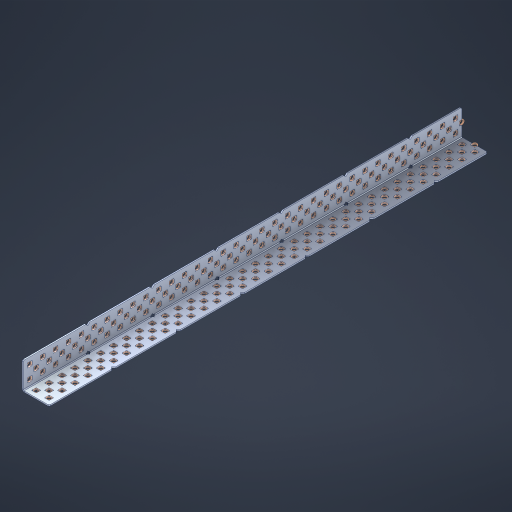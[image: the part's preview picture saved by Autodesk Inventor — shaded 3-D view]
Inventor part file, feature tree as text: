
AUTODESK INVENTOR PART (.ipt)
format: ipt  version: 2023 (Build 270158000, 158)  size: 2,273,792 bytes
history: native  units: in
note: dims shown in document units (in); Inventor stores cm internally (conversion verified against a paired STEP export)
features: other x210, extrude x202, sheet_metal_op x8, sketch x7, pattern_linear x2, mirror x1, chamfer x1
ambient origin geometry x8: Origin, YZ Plane, XZ Plane, XY Plane, X Axis, Y Axis, Z Axis, Center Point
bodies: Solid1 (feature_tree), Body (feature_tree)
feature tree (431):
  sheet_metal_op  "Flanges"
  sheet_metal_op  "Body Pattern"
  pattern_linear  "Center Pattern"  Spacing1=1.0in  [1 undecoded]
  other  "Arc Length"
  pattern_linear  "Notch Pattern"  Spacing1=0.1875in  [1 undecoded]
  other  "Diagonal Plane"
  mirror  "Everything Mirrored"
  chamfer  "End Chamfer"
  sketch  "Sketch1"  dims[d0=1.0in]
  other  "Plate1"
  sketch  "Sketch2"  dims[d1=17.0in]
  other  "Plate2"
  sheet_metal_op  "Bend1"
  sheet_metal_op  "Corner1"
  sketch  "Sketch8"  dims[d2=0.0469in]
  sketch  "Sketch9"  dims[d3=0.0469in]
  other  "Srf91"
  sheet_metal_op  "Body Pattern Sketch"
  other  "Srf92"
  sketch  "Sketch13"  dims[d4=0.0234in]
  sketch  "Sketch15"  dims[d5=0.0938in]
  sketch  "Sketch16"  dims[d6=0.0469in d7=1.0in d8=90.0deg d9=0.0312in d10=0.1875in d11=0.0469in d12=0.0469in d49=0.182in d50=0.02in d52=0.25in d53=0.0469in d54=0.0in d55=0.172in d56=1.0in d57=0.0in d60=13.3858in d62=0.5in d63=0.7874in d65=0.5in d85=0.1473in d86=0.1659in d89=0.0469in d90=0.0in d91=0.04in d92=0.0491in d95=2.5in d96=0.04in d97=0.25in d98=45.0deg d99=0.25in d106=0.182in d107=0.02in d108=0.5in d110=0.0469in d111=0.0in d112=0.172in d113=0.5in d114=0.0in d117=0.5in d123=0.25in d125=0.25in d126=0.0491in d127=0.1227in d128=0.08in d129=0.04in d130=2.5in]
  other  "Srf786"
  other  "Srf856"
  other  "Srf857"
  other  "Srf858"
  other  "Srf859"
  other  "Srf860"
  other  "Srf861"
  other  "Srf889"
  other  "Srf890"
  other  "Srf891"
  other  "Srf1275"
  other  "Srf1276"
  other  "Srf1278"
  other  "Srf1279"
  other  "Srf1280"
  other  "Srf1281"
  other  "Srf1282"
  other  "Srf1283"
  other  "Srf1277"
  other  "Srf1285"
  other  "Srf1286"
  other  "Srf1287"
  other  "Srf1383"
  other  "Srf1384"
  other  "Srf1385"
  other  "Srf1386"
  other  "Srf1387"
  other  "Srf1388"
  other  "Srf1389"
  other  "Srf1390"
  other  "Srf1391"
  other  "Srf1392"
  other  "Srf1393"
  other  "Srf1394"
  other  "Srf1395"
  other  "Srf1396"
  other  "Srf1397"
  other  "Srf1398"
  other  "Srf1399"
  other  "Srf1400"
  other  "Srf1401"
  other  "Srf1402"
  other  "Srf1403"
  other  "Srf1404"
  other  "Srf1405"
  other  "Srf1406"
  other  "Srf1407"
  other  "Srf1408"
  other  "Srf1409"
  other  "Srf1410"
  other  "Srf1411"
  other  "Srf1412"
  other  "Srf1413"
  other  "Srf1414"
  other  "Srf1415"
  other  "Srf1416"
  other  "Srf1417"
  other  "Srf1418"
  other  "Srf1419"
  other  "Srf1420"
  other  "Srf1421"
  other  "Srf1422"
  other  "Srf1423"
  other  "Srf1424"
  other  "Srf1425"
  other  "Srf1426"
  other  "Srf1427"
  other  "Srf1428"
  other  "Srf1429"
  other  "Srf1430"
  other  "Srf1431"
  other  "Srf1432"
  other  "Srf1433"
  other  "Srf1434"
  other  "Srf1435"
  other  "Srf1436"
  other  "Srf1437"
  other  "Srf1438"
  other  "Srf1439"
  other  "Srf1440"
  other  "Srf1441"
  other  "Srf1442"
  other  "Srf1445"
  other  "Srf1446"
  other  "Srf1447"
  other  "Srf1448"
  other  "Srf1449"
  other  "Srf1450"
  other  "Srf1451"
  other  "Srf1452"
  other  "Srf1453"
  other  "Srf1454"
  other  "Srf1455"
  other  "Srf1456"
  other  "Srf1457"
  other  "Srf1458"
  other  "Srf1459"
  other  "Srf1460"
  other  "Srf1461"
  other  "Srf1462"
  other  "Srf1463"
  other  "Srf1464"
  other  "Srf1465"
  other  "Srf1466"
  other  "Srf1467"
  other  "Srf1468"
  other  "Srf1469"
  other  "Srf1470"
  other  "Srf1471"
  other  "Srf1472"
  other  "Srf1473"
  other  "Srf1474"
  other  "Srf1475"
  other  "Srf1476"
  other  "Srf1477"
  other  "Srf1478"
  other  "Srf1479"
  other  "Srf1480"
  other  "Srf1481"
  other  "Srf1482"
  other  "Srf1483"
  other  "Srf1484"
  other  "Srf1485"
  other  "Srf1486"
  other  "Srf1487"
  other  "Srf1488"
  other  "Srf1489"
  other  "Srf1490"
  other  "Srf1491"
  other  "Srf1492"
  other  "Srf1493"
  other  "Srf1494"
  other  "Srf1495"
  other  "Srf1496"
  other  "Srf1497"
  other  "Srf1498"
  other  "Srf1499"
  other  "Srf1500"
  other  "Srf1501"
  other  "Srf1502"
  other  "Srf1503"
  other  "Srf1504"
  other  "Srf1505"
  other  "Srf1506"
  other  "Srf1507"
  other  "Srf1508"
  other  "Srf1509"
  other  "Srf1510"
  other  "Srf1511"
  other  "Srf1512"
  other  "Srf1513"
  other  "Srf1514"
  other  "Srf1515"
  other  "Srf1516"
  other  "Srf1517"
  other  "Srf1518"
  other  "Srf1519"
  other  "Srf1520"
  other  "Srf1521"
  other  "Srf1522"
  other  "Srf1523"
  other  "Srf1524"
  other  "Srf1525"
  other  "Srf1526"
  other  "Srf1527"
  other  "Srf1528"
  other  "Srf1529"
  other  "Srf1530"
  other  "Srf1531"
  other  "Srf1532"
  other  "Srf1533"
  other  "Srf1534"
  other  "Srf1537"
  other  "Srf1538"
  other  "Srf1539"
  other  "Srf1540"
  other  "Srf1541"
  other  "Srf1542"
  other  "Srf1543"
  other  "Srf1544"
  other  "Srf1545"
  other  "Srf1546"
  other  "Srf1547"
  other  "Srf1548"
  other  "Srf1549"
  other  "Srf1550"
  other  "Srf1551"
  other  "Srf1552"
  other  "Srf1553"
  other  "Srf1554"
  other  "Srf1555"
  other  "Srf1556"
  other  "Srf1557"
  other  "Srf1558"
  other  "Srf1559"
  other  "Srf1560"
  other  "Srf1561"
  other  "Srf1562"
  other  "Srf1563"
  other  "Srf1564"
  other  "Srf1565"
  other  "Srf1566"
  sheet_metal_op  "Body Stamp"
  sheet_metal_op  "Body Circle"
  other  "Center Stamp"
  other  "Center Circle"
  sheet_metal_op  "Notch"
  extrude  "ExtrusionSrf92"  Depth=0.0469in
  extrude  "ExtrusionSrf856"  Depth=0.0469in
  extrude  "ExtrusionSrf857"  Depth=0.182in
  extrude  "ExtrusionSrf858"  Depth=0.02in
  extrude  "ExtrusionSrf859"  Depth=0.25in
  extrude  "ExtrusionSrf860"  Depth=0.0469in
  extrude  "ExtrusionSrf861"  TaperAngle=0.0deg  [1 undecoded]
  extrude  "ExtrusionSrf889"  Depth=2.5in
  extrude  "ExtrusionSrf890"  Depth=1.0in TaperAngle=0.0deg
  extrude  "ExtrusionSrf891"  Depth=2.5in
  extrude  "ExtrusionSrf1275"  Depth=0.5in
  extrude  "ExtrusionSrf1276"  Depth=2.5in
  extrude  "ExtrusionSrf1277"  Depth=2.5in
  extrude  "ExtrusionSrf1278"  Depth=0.0469in
  extrude  "ExtrusionSrf1279"  Depth=2.5in TaperAngle=0.0deg
  extrude  "ExtrusionSrf1280"  Depth=2.5in
  extrude  "ExtrusionSrf1281"  Depth=0.25in TaperAngle=45.0deg
  extrude  "ExtrusionSrf1282"  Depth=0.25in
  extrude  "ExtrusionSrf1345"  Depth=0.182in
  extrude  "ExtrusionSrf1346"  Depth=0.02in
  extrude  "ExtrusionSrf1347"  Depth=0.5in
  extrude  "ExtrusionSrf1348"  Depth=0.0469in
  extrude  "ExtrusionSrf1383"  TaperAngle=0.0deg  [1 undecoded]
  extrude  "ExtrusionSrf1384"  Depth=2.5in
  extrude  "ExtrusionSrf1385"  Depth=0.5in TaperAngle=0.0deg
  extrude  "ExtrusionSrf1386"  Depth=0.5in
  extrude  "ExtrusionSrf1387"  Depth=0.25in
  extrude  "ExtrusionSrf1388"  Depth=0.25in
  extrude  "ExtrusionSrf1389"  Depth=2.5in
  extrude  "ExtrusionSrf1390"  Depth=2.5in
  extrude  "ExtrusionSrf1391"  Depth=2.5in
  extrude  "ExtrusionSrf1392"  Depth=2.5in
  extrude  "ExtrusionSrf1393"  Depth=2.5in
  extrude  "ExtrusionSrf1394"  [1 undecoded]
  extrude  "ExtrusionSrf1395"  [1 undecoded]
  extrude  "ExtrusionSrf1396"  [1 undecoded]
  extrude  "ExtrusionSrf1397"  [1 undecoded]
  extrude  "ExtrusionSrf1398"  [1 undecoded]
  extrude  "ExtrusionSrf1399"  [1 undecoded]
  extrude  "ExtrusionSrf1400"  [1 undecoded]
  extrude  "ExtrusionSrf1401"  [1 undecoded]
  extrude  "ExtrusionSrf1402"  [1 undecoded]
  extrude  "ExtrusionSrf1403"  [1 undecoded]
  extrude  "ExtrusionSrf1404"  [1 undecoded]
  extrude  "ExtrusionSrf1405"  [1 undecoded]
  extrude  "ExtrusionSrf1406"  [1 undecoded]
  extrude  "ExtrusionSrf1407"  [1 undecoded]
  extrude  "ExtrusionSrf1408"  [1 undecoded]
  extrude  "ExtrusionSrf1409"  [1 undecoded]
  extrude  "ExtrusionSrf1410"  [1 undecoded]
  extrude  "ExtrusionSrf1411"  [1 undecoded]
  extrude  "ExtrusionSrf1412"  [1 undecoded]
  extrude  "ExtrusionSrf1413"  [1 undecoded]
  extrude  "ExtrusionSrf1414"  [1 undecoded]
  extrude  "ExtrusionSrf1415"  [1 undecoded]
  extrude  "ExtrusionSrf1416"  [1 undecoded]
  extrude  "ExtrusionSrf1417"  [1 undecoded]
  extrude  "ExtrusionSrf1418"  [1 undecoded]
  extrude  "ExtrusionSrf1419"  [1 undecoded]
  extrude  "ExtrusionSrf1420"  [1 undecoded]
  extrude  "ExtrusionSrf1421"  [1 undecoded]
  extrude  "ExtrusionSrf1422"  [1 undecoded]
  extrude  "ExtrusionSrf1423"  [1 undecoded]
  extrude  "ExtrusionSrf1424"  [1 undecoded]
  extrude  "ExtrusionSrf1425"  [1 undecoded]
  extrude  "ExtrusionSrf1426"  [1 undecoded]
  extrude  "ExtrusionSrf1427"  [1 undecoded]
  extrude  "ExtrusionSrf1428"  [1 undecoded]
  extrude  "ExtrusionSrf1429"  [1 undecoded]
  extrude  "ExtrusionSrf1430"  [1 undecoded]
  extrude  "ExtrusionSrf1431"  [1 undecoded]
  extrude  "ExtrusionSrf1432"  [1 undecoded]
  extrude  "ExtrusionSrf1433"  [1 undecoded]
  extrude  "ExtrusionSrf1434"  [1 undecoded]
  extrude  "ExtrusionSrf1435"  [1 undecoded]
  extrude  "ExtrusionSrf1436"  [1 undecoded]
  extrude  "ExtrusionSrf1437"  [1 undecoded]
  extrude  "ExtrusionSrf1438"  [1 undecoded]
  extrude  "ExtrusionSrf1439"  [1 undecoded]
  extrude  "ExtrusionSrf1440"  [1 undecoded]
  extrude  "ExtrusionSrf1441"  [1 undecoded]
  extrude  "ExtrusionSrf1442"  [1 undecoded]
  extrude  "ExtrusionSrf1445"  [1 undecoded]
  extrude  "ExtrusionSrf1446"  [1 undecoded]
  extrude  "ExtrusionSrf1447"  [1 undecoded]
  extrude  "ExtrusionSrf1448"  [1 undecoded]
  extrude  "ExtrusionSrf1449"  [1 undecoded]
  extrude  "ExtrusionSrf1450"  [1 undecoded]
  extrude  "ExtrusionSrf1451"  [1 undecoded]
  extrude  "ExtrusionSrf1452"  [1 undecoded]
  extrude  "ExtrusionSrf1453"  [1 undecoded]
  extrude  "ExtrusionSrf1454"  [1 undecoded]
  extrude  "ExtrusionSrf1455"  [1 undecoded]
  extrude  "ExtrusionSrf1456"  [1 undecoded]
  extrude  "ExtrusionSrf1457"  [1 undecoded]
  extrude  "ExtrusionSrf1458"  [1 undecoded]
  extrude  "ExtrusionSrf1459"  [1 undecoded]
  extrude  "ExtrusionSrf1460"  [1 undecoded]
  extrude  "ExtrusionSrf1461"  [1 undecoded]
  extrude  "ExtrusionSrf1462"  [1 undecoded]
  extrude  "ExtrusionSrf1463"  [1 undecoded]
  extrude  "ExtrusionSrf1464"  [1 undecoded]
  extrude  "ExtrusionSrf1465"  [1 undecoded]
  extrude  "ExtrusionSrf1466"  [1 undecoded]
  extrude  "ExtrusionSrf1467"  [1 undecoded]
  extrude  "ExtrusionSrf1468"  [1 undecoded]
  extrude  "ExtrusionSrf1469"  [1 undecoded]
  extrude  "ExtrusionSrf1470"  [1 undecoded]
  extrude  "ExtrusionSrf1471"  [1 undecoded]
  extrude  "ExtrusionSrf1472"  [1 undecoded]
  extrude  "ExtrusionSrf1473"  [1 undecoded]
  extrude  "ExtrusionSrf1474"  [1 undecoded]
  extrude  "ExtrusionSrf1475"  [1 undecoded]
  extrude  "ExtrusionSrf1476"  [1 undecoded]
  extrude  "ExtrusionSrf1477"  [1 undecoded]
  extrude  "ExtrusionSrf1478"  [1 undecoded]
  extrude  "ExtrusionSrf1479"  [1 undecoded]
  extrude  "ExtrusionSrf1480"  [1 undecoded]
  extrude  "ExtrusionSrf1481"  [1 undecoded]
  extrude  "ExtrusionSrf1482"  [1 undecoded]
  extrude  "ExtrusionSrf1483"  [1 undecoded]
  extrude  "ExtrusionSrf1484"  [1 undecoded]
  extrude  "ExtrusionSrf1485"  [1 undecoded]
  extrude  "ExtrusionSrf1486"  [1 undecoded]
  extrude  "ExtrusionSrf1487"  [1 undecoded]
  extrude  "ExtrusionSrf1488"  [1 undecoded]
  extrude  "ExtrusionSrf1489"  [1 undecoded]
  extrude  "ExtrusionSrf1490"  [1 undecoded]
  extrude  "ExtrusionSrf1491"  [1 undecoded]
  extrude  "ExtrusionSrf1492"  [1 undecoded]
  extrude  "ExtrusionSrf1493"  [1 undecoded]
  extrude  "ExtrusionSrf1494"  [1 undecoded]
  extrude  "ExtrusionSrf1495"  [1 undecoded]
  extrude  "ExtrusionSrf1496"  [1 undecoded]
  extrude  "ExtrusionSrf1497"  [1 undecoded]
  extrude  "ExtrusionSrf1498"  [1 undecoded]
  extrude  "ExtrusionSrf1499"  [1 undecoded]
  extrude  "ExtrusionSrf1500"  [1 undecoded]
  extrude  "ExtrusionSrf1501"  [1 undecoded]
  extrude  "ExtrusionSrf1502"  [1 undecoded]
  extrude  "ExtrusionSrf1503"  [1 undecoded]
  extrude  "ExtrusionSrf1504"  [1 undecoded]
  extrude  "ExtrusionSrf1505"  [1 undecoded]
  extrude  "ExtrusionSrf1506"  [1 undecoded]
  extrude  "ExtrusionSrf1507"  [1 undecoded]
  extrude  "ExtrusionSrf1508"  [1 undecoded]
  extrude  "ExtrusionSrf1509"  [1 undecoded]
  extrude  "ExtrusionSrf1510"  [1 undecoded]
  extrude  "ExtrusionSrf1511"  [1 undecoded]
  extrude  "ExtrusionSrf1512"  [1 undecoded]
  extrude  "ExtrusionSrf1513"  [1 undecoded]
  extrude  "ExtrusionSrf1514"  [1 undecoded]
  extrude  "ExtrusionSrf1515"  [1 undecoded]
  extrude  "ExtrusionSrf1516"  [1 undecoded]
  extrude  "ExtrusionSrf1517"  [1 undecoded]
  extrude  "ExtrusionSrf1518"  [1 undecoded]
  extrude  "ExtrusionSrf1519"  [1 undecoded]
  extrude  "ExtrusionSrf1520"  [1 undecoded]
  extrude  "ExtrusionSrf1521"  [1 undecoded]
  extrude  "ExtrusionSrf1522"  [1 undecoded]
  extrude  "ExtrusionSrf1523"  [1 undecoded]
  extrude  "ExtrusionSrf1524"  [1 undecoded]
  extrude  "ExtrusionSrf1525"  [1 undecoded]
  extrude  "ExtrusionSrf1526"  [1 undecoded]
  extrude  "ExtrusionSrf1527"  [1 undecoded]
  extrude  "ExtrusionSrf1528"  [1 undecoded]
  extrude  "ExtrusionSrf1529"  [1 undecoded]
  extrude  "ExtrusionSrf1530"  [1 undecoded]
  extrude  "ExtrusionSrf1531"  [1 undecoded]
  extrude  "ExtrusionSrf1532"  [1 undecoded]
  extrude  "ExtrusionSrf1533"  [1 undecoded]
  extrude  "ExtrusionSrf1534"  [1 undecoded]
  extrude  "ExtrusionSrf1537"  [1 undecoded]
  extrude  "ExtrusionSrf1538"  [1 undecoded]
  extrude  "ExtrusionSrf1539"  [1 undecoded]
  extrude  "ExtrusionSrf1540"  [1 undecoded]
  extrude  "ExtrusionSrf1541"  [1 undecoded]
  extrude  "ExtrusionSrf1542"  [1 undecoded]
  extrude  "ExtrusionSrf1543"  [1 undecoded]
  extrude  "ExtrusionSrf1544"  [1 undecoded]
  extrude  "ExtrusionSrf1545"  [1 undecoded]
  extrude  "ExtrusionSrf1546"  [1 undecoded]
  extrude  "ExtrusionSrf1547"  [1 undecoded]
  extrude  "ExtrusionSrf1548"  [1 undecoded]
  extrude  "ExtrusionSrf1549"  [1 undecoded]
  extrude  "ExtrusionSrf1550"  [1 undecoded]
  extrude  "ExtrusionSrf1551"  [1 undecoded]
  extrude  "ExtrusionSrf1552"  [1 undecoded]
  extrude  "ExtrusionSrf1553"  [1 undecoded]
  extrude  "ExtrusionSrf1554"  [1 undecoded]
  extrude  "ExtrusionSrf1555"  [1 undecoded]
  extrude  "ExtrusionSrf1556"  [1 undecoded]
  extrude  "ExtrusionSrf1557"  [1 undecoded]
  extrude  "ExtrusionSrf1558"  [1 undecoded]
  extrude  "ExtrusionSrf1559"  [1 undecoded]
  extrude  "ExtrusionSrf1560"  [1 undecoded]
  extrude  "ExtrusionSrf1561"  [1 undecoded]
  extrude  "ExtrusionSrf1562"  [1 undecoded]
  extrude  "ExtrusionSrf1563"  [1 undecoded]
  extrude  "ExtrusionSrf1564"  [1 undecoded]
  extrude  "ExtrusionSrf1565"  [1 undecoded]
  extrude  "ExtrusionSrf1566"  [1 undecoded]
note: 173 required parameter values undecoded (feature->parameter linkage not recoverable at this tier; creation-order binding heuristic only, values carry confidence <= 0.55)
